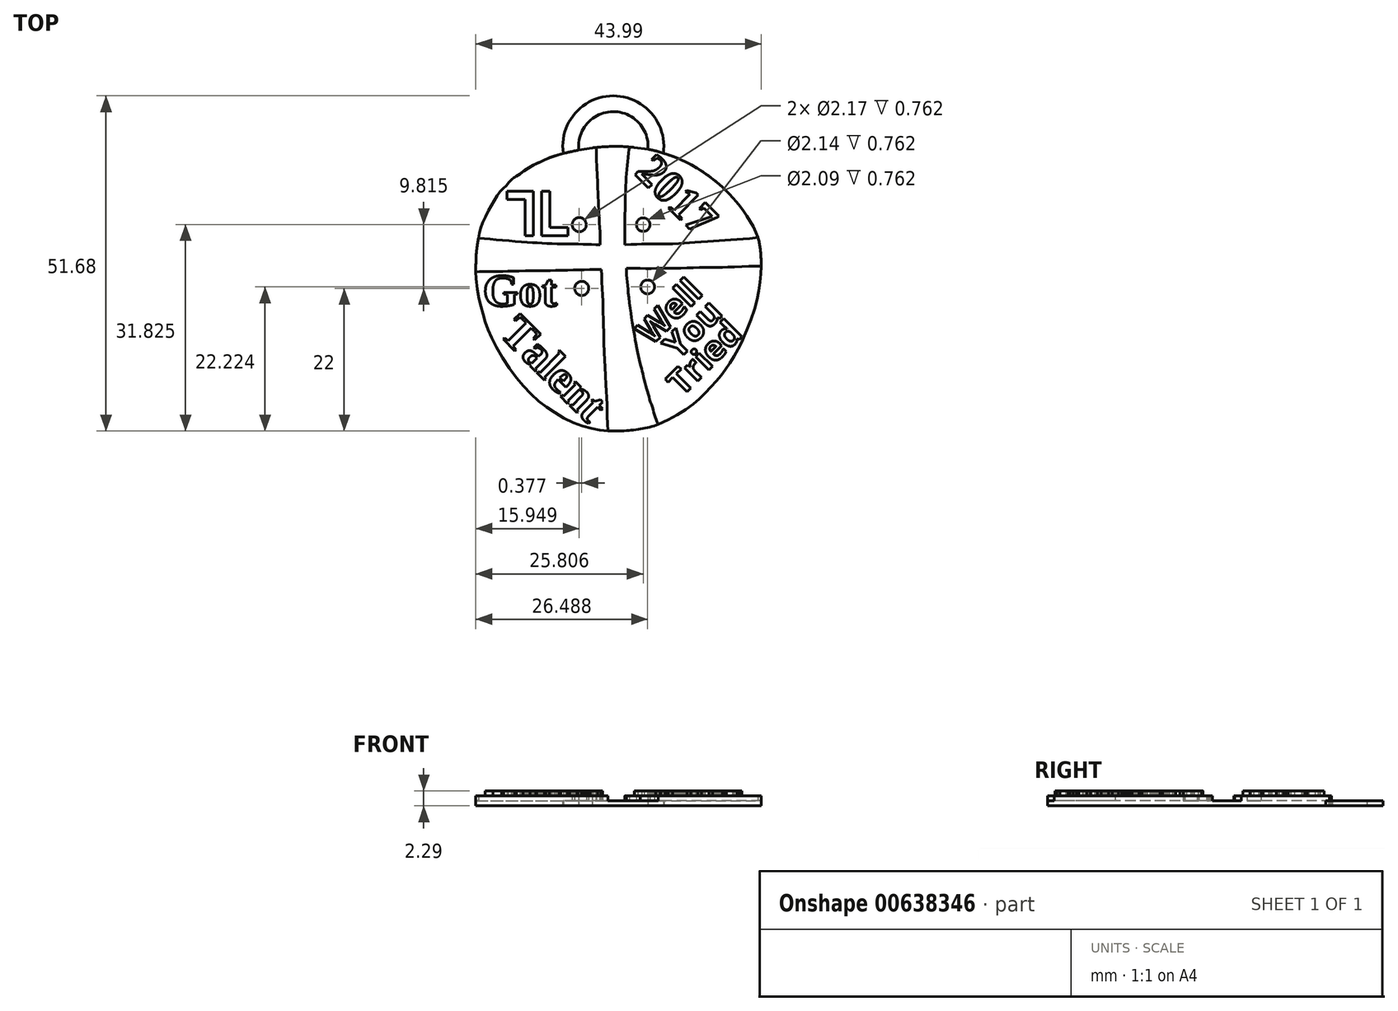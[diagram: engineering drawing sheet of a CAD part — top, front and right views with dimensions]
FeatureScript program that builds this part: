
annotation { "Feature Type Name" : "Feature", "Feature Type Description" : "" }
export const myFeature = defineFeature(function(context is Context, id is Id, definition is map)
    precondition{}
    {
        {
            var Q0;
            Q0=qCreatedBy(makeId("Top.planeOp"),FACE);
            var sketch = newSketch(context, id + "F0", { "sketchPlane" : qUnion([Q0])});
            skFitSpline(sketch, "E0", {"points": [v(-3.2, 18.94) * mm, v(-4.93, 18.73) * mm, v(-6.65, 18.38) * mm, v(-9.43, 17.71) * mm, v(-11.65, 16.8) * mm, v(-13.81, 15.7) * mm, v(-15.1, 14.79) * mm, v(-16.18, 14.06) * mm, v(-17.11, 13.04) * mm, v(-17.93, 12.28) * mm, v(-18.93, 10.84) * mm, v(-20, 8.91) * mm, v(-21.03, 6.49) * mm, v(-21.4, 4.95) * mm, v(-21.72, 2.6) * mm, v(-21.8, -0.22) * mm, v(-21.8, -0.23) * mm, v(-21.8, -0.23) * mm, v(-21.71, -1.8) * mm, v(-21.3, -4.51) * mm, v(-20.89, -6.04) * mm, v(-20.44, -7.64) * mm, v(-19.78, -9.41) * mm, v(-18.74, -11.67) * mm, v(-16.55, -15.21) * mm, v(-14.5, -17.79) * mm, v(-12.27, -20.05) * mm, v(-10.29, -21.5) * mm, v(-7.75, -23.03) * mm, v(-5.32, -24.04) * mm, v(-3.1, -24.6) * mm, v(-1.46, -24.77) * mm, v(2.16, -24.67) * mm, v(6.33, -23.76) * mm, v(9.35, -22.24) * mm, v(11.68, -20.7) * mm, v(13.1, -19.42) * mm, v(14.6, -17.86) * mm, v(15.74, -16.57) * mm, v(16.74, -15.22) * mm, v(17.75, -13.69) * mm, v(18.76, -11.92) * mm, v(19.49, -10.42) * mm, v(19.9, -9.38) * mm, v(21.17, -6.04) * mm, v(21.77, -3.53) * mm, v(22.08, -1.28) * mm, v(22.19, 0.62) * mm, v(22.1, 2.84) * mm, v(21.68, 5.05) * mm, v(20.34, 7.8) * mm, v(18.56, 10.32) * mm, v(16.99, 12.01) * mm, v(15.7, 13.25) * mm, v(13.81, 14.73) * mm, v(11.03, 16.46) * mm, v(8.11, 17.71) * mm, v(5.13, 18.58) * mm, v(1.93, 19) * mm, v(-0.6, 19.1) * mm, v(-3.2, 18.94) * mm]});
            skArc(sketch, "E1", {"start": v(4.73, 18.66) * mm, "mid": v(-0.67, 24.46) * mm, "end": v(-5.93, 18.54) * mm});
            skArc(sketch, "E2", {"start": v(7.1, 18.06) * mm, "mid": v(-0.63, 26.9) * mm, "end": v(-8.32, 18.01) * mm});
            skLineSegment(sketch, "E3", {"start": v(-5.93, 18.54) * mm, "end": v(-3.82, 18.88) * mm});
            skLineSegment(sketch, "E4", {"start": v(2.6, 18.94) * mm, "end": v(4.73, 18.66) * mm});
            skSolve(sketch);
        }
        {
            var Q0;
            Q0 = qSketchRegion(id + "F0", true);
            extrude(context, id + "F1", {"entities" : qUnion([Q0]), "depth" : 0.76 * mm, "offsetDistance" : 25.4 * mm});
        }
        {
            var Q0;
            Q0=makeQuery(id+"F1.opExtrude","CAP_FACE",FACE,{"disambiguationData":[OSD([sQuery(id+"F0.wireOp",EDGE,"E0")])],"isStart":false});
            var sketch = newSketch(context, id + "F2", { "sketchPlane" : qUnion([Q0])});
            skFitSpline(sketch, "E5", {"points": [v(-3.2, 18.94) * mm, v(-4.93, 18.73) * mm, v(-6.65, 18.38) * mm, v(-9.43, 17.71) * mm, v(-11.65, 16.8) * mm, v(-13.81, 15.7) * mm, v(-15.1, 14.79) * mm, v(-16.18, 14.06) * mm, v(-17.11, 13.04) * mm, v(-17.93, 12.28) * mm, v(-18.93, 10.84) * mm, v(-20, 8.91) * mm, v(-21.03, 6.49) * mm, v(-21.4, 4.95) * mm, v(-21.72, 2.6) * mm, v(-21.8, -0.22) * mm, v(-21.8, -0.23) * mm, v(-21.8, -0.23) * mm, v(-21.71, -1.8) * mm, v(-21.3, -4.51) * mm, v(-20.89, -6.04) * mm, v(-20.44, -7.64) * mm, v(-19.78, -9.41) * mm, v(-18.74, -11.67) * mm, v(-16.55, -15.21) * mm, v(-14.5, -17.79) * mm, v(-12.27, -20.05) * mm, v(-10.29, -21.5) * mm, v(-7.75, -23.03) * mm, v(-5.32, -24.04) * mm, v(-3.1, -24.6) * mm, v(-1.46, -24.77) * mm, v(2.16, -24.67) * mm, v(6.33, -23.76) * mm, v(9.35, -22.24) * mm, v(11.68, -20.7) * mm, v(13.1, -19.42) * mm, v(14.6, -17.86) * mm, v(15.74, -16.57) * mm, v(16.74, -15.22) * mm, v(17.75, -13.69) * mm, v(18.76, -11.92) * mm, v(19.49, -10.42) * mm, v(19.9, -9.38) * mm, v(21.17, -6.04) * mm, v(21.77, -3.53) * mm, v(22.08, -1.28) * mm, v(22.19, 0.62) * mm, v(22.1, 2.84) * mm, v(21.68, 5.05) * mm, v(20.34, 7.8) * mm, v(18.56, 10.32) * mm, v(16.99, 12.01) * mm, v(15.7, 13.25) * mm, v(13.81, 14.73) * mm, v(11.03, 16.46) * mm, v(8.11, 17.71) * mm, v(5.13, 18.58) * mm, v(1.93, 19) * mm, v(-0.6, 19.1) * mm, v(-3.2, 18.94) * mm]});
            skFitSpline(sketch, "E6", {"points": [v(-21.4, 4.95) * mm, v(-17.9, 4.65) * mm, v(-14.1, 4.33) * mm, v(-11.67, 4.19) * mm, v(-9.21, 4.07) * mm, v(-6.38, 4.04) * mm, v(-4.4, 3.98) * mm, v(-2.64, 3.92) * mm], "startDerivative": vector(20.38, -1.44) * mm, "endDerivative": vector(15, -0.48) * mm});
            skFitSpline(sketch, "E7", {"points": [v(-3.2, 18.94) * mm, v(-3.2, 16.96) * mm, v(-3.11, 15.45) * mm, v(-3.05, 14.12) * mm, v(-3, 12.68) * mm, v(-2.92, 11) * mm, v(-2.83, 9.25) * mm, v(-2.75, 7.56) * mm, v(-2.65, 5.66) * mm, v(-2.64, 3.92) * mm], "startDerivative": vector(-0.27, -16.84) * mm, "endDerivative": vector(-0.12, -15.04) * mm});
            skFitSpline(sketch, "E8", {"points": [v(1.93, 19) * mm, v(1.79, 18.41) * mm, v(1.61, 17.07) * mm, v(1.52, 15.95) * mm, v(1.4, 14.63) * mm, v(1.34, 13.3) * mm, v(1.25, 11.63) * mm, v(1.23, 9.85) * mm, v(1.17, 8.24) * mm, v(1.17, 6.74) * mm, v(1.17, 5.24) * mm, v(1.18, 3.92) * mm], "startDerivative": vector(-2.33, -8.47) * mm, "endDerivative": vector(0.1, -14.43) * mm});
            skFitSpline(sketch, "E9", {"points": [v(1.18, 3.92) * mm, v(2.92, 4) * mm, v(4.2, 4.03) * mm, v(5.44, 4.03) * mm, v(7.88, 4.06) * mm, v(9.82, 4.15) * mm, v(11.19, 4.25) * mm, v(12.96, 4.38) * mm, v(14.85, 4.5) * mm, v(16.43, 4.6) * mm, v(18.1, 4.74) * mm, v(20.21, 4.87) * mm, v(21.53, 5.02) * mm, v(21.68, 5.05) * mm], "startDerivative": vector(21.76, 1.06) * mm, "endDerivative": vector(6, 0.77) * mm});
            skFitSpline(sketch, "E10", {"points": [v(-21.8, -0.23) * mm, v(-20.73, -0.17) * mm, v(-19.36, -0.18) * mm, v(-17.32, -0.17) * mm, v(-15.12, -0.1) * mm, v(-11.79, -0.04) * mm, v(-9.68, -0.04) * mm, v(-7.15, 0.04) * mm, v(-4.95, 0.09) * mm, v(-2.43, 0.14) * mm], "startDerivative": vector(13.2, 1.01) * mm, "endDerivative": vector(20.6, 0.3) * mm});
            skFitSpline(sketch, "E11", {"points": [v(-2.43, 0.14) * mm, v(-2.36, -1.12) * mm, v(-2.35, -2.44) * mm, v(-2.28, -3.8) * mm, v(-2.22, -5.07) * mm, v(-2.23, -6.07) * mm, v(-2.18, -7.24) * mm, v(-2.13, -8.33) * mm, v(-2.04, -11.03) * mm, v(-1.94, -13.54) * mm, v(-1.87, -15.22) * mm, v(-1.74, -17.82) * mm, v(-1.65, -19.04) * mm, v(-1.6, -20.63) * mm, v(-1.57, -21.68) * mm, v(-1.5, -23.09) * mm, v(-1.46, -24.77) * mm], "startDerivative": vector(1.33, -22) * mm, "endDerivative": vector(0.62, -25.83) * mm});
            skFitSpline(sketch, "E12", {"points": [v(22.19, 0.62) * mm, v(20.29, 0.62) * mm, v(17.64, 0.5) * mm, v(15.92, 0.43) * mm, v(14.34, 0.42) * mm, v(12.48, 0.43) * mm, v(10.51, 0.34) * mm, v(8.76, 0.3) * mm, v(6.65, 0.3) * mm, v(5.13, 0.27) * mm, v(3.59, 0.28) * mm, v(2.45, 0.28) * mm, v(1.42, 0.28) * mm], "startDerivative": vector(-20.3, 0.28) * mm, "endDerivative": vector(-15.78, 0.1) * mm});
            skFitSpline(sketch, "E13", {"points": [v(1.42, 0.28) * mm, v(1.42, -0.35) * mm, v(1.5, -1.26) * mm, v(1.57, -2) * mm, v(1.65, -2.85) * mm, v(1.76, -4.02) * mm, v(2, -5.84) * mm, v(2.2, -7.42) * mm, v(2.47, -8.84) * mm, v(2.7, -10.17) * mm, v(2.86, -11.2) * mm, v(3.1, -12.38) * mm, v(3.31, -13.4) * mm, v(3.5, -14.38) * mm], "startDerivative": vector(-0.27, -10.35) * mm, "endDerivative": vector(4.5, -12.84) * mm});
            skFitSpline(sketch, "E14", {"points": [v(3.5, -14.38) * mm, v(3.8, -15.37) * mm, v(4.04, -16.41) * mm, v(4.42, -17.84) * mm, v(4.77, -18.95) * mm, v(5.03, -20.03) * mm, v(5.37, -21.02) * mm, v(5.67, -22.04) * mm, v(5.91, -22.82) * mm, v(6.33, -23.76) * mm], "startDerivative": vector(2.84, -9.2) * mm, "endDerivative": vector(4.17, -8.96) * mm});
            skCircle(sketch, "E15", {"center": v(-5.85, 7.03) * mm, "radius": 1.09 * mm});
            skCircle(sketch, "E16", {"center": v(4, 7.04) * mm, "radius": 1.05 * mm});
            skCircle(sketch, "E17", {"center": v(4.69, -2.57) * mm, "radius": 1.07 * mm});
            skCircle(sketch, "E18", {"center": v(-5.47, -2.79) * mm, "radius": 1.08 * mm});
            skSolve(sketch);
        }
        {
            var Q0;
            {var subQ0=sQuery(id+"F2.wireOp",EDGE,"E6");Q0=makeQuery(id+"F2.imprint","IMPRINT",FACE,{"disambiguationData":[TD([[makeQuery(id+"F2.imprint","IMPRINT",EDGE,{"derivedFrom":subQ0}),1.0]])]});}
            var Q1;
            {var subQ0=sQuery(id+"F2.wireOp",EDGE,"E8");Q1=makeQuery(id+"F2.imprint","IMPRINT",FACE,{"disambiguationData":[TD([[makeQuery(id+"F2.imprint","IMPRINT",EDGE,{"derivedFrom":subQ0}),1.0]])]});}
            var Q2;
            {var subQ1=sQuery(id+"F2.wireOp",EDGE,"E12");Q2=makeQuery(id+"F2.imprint","IMPRINT",FACE,{"disambiguationData":[TD([[makeQuery(id+"F2.imprint","IMPRINT",EDGE,{"derivedFrom":subQ1}),1.0]])]});}
            var Q3;
            {var subQ0=sQuery(id+"F2.wireOp",EDGE,"E10");Q3=makeQuery(id+"F2.imprint","IMPRINT",FACE,{"disambiguationData":[TD([[makeQuery(id+"F2.imprint","IMPRINT",EDGE,{"derivedFrom":subQ0}),-1.0]])]});}
            extrude(context, id + "F3", {"entities" : qUnion([Q0, Q1, Q2, Q3]), "operationType" : NewBodyOperationType.ADD, "depth" : 0.76 * mm, "offsetDistance" : 25.4 * mm});
        }
        {
            var Q0;
            Q0=makeQuery(id+"F3.opExtrude","CAP_FACE",FACE,{"disambiguationData":[OSD([sQuery(id+"F2.wireOp",EDGE,"E5"),sQuery(id+"F2.wireOp",EDGE,"E8"),sQuery(id+"F2.wireOp",EDGE,"E9"),sQuery(id+"F2.wireOp",EDGE,"E16")])],"isStart":false});
            var sketch = newSketch(context, id + "F4", { "sketchPlane" : qUnion([Q0])});
            skText(sketch, "E19", { "text": "2017", "fontName": "Tinos-Bold.ttf"});
            const initialGuessF4  = {"E19": [0.00254, 0.01496, 0.7071, -0.7071, 0.00508]};
            skSetInitialGuess(sketch, initialGuessF4);
            skSolve(sketch);
        }
        {
            var Q0;
            Q0=makeQuery(id+"F3.opExtrude","CAP_FACE",FACE,{"disambiguationData":[OSD([sQuery(id+"F2.wireOp",EDGE,"E5"),sQuery(id+"F2.wireOp",EDGE,"E10"),sQuery(id+"F2.wireOp",EDGE,"E11"),sQuery(id+"F2.wireOp",EDGE,"E18")])],"isStart":false});
            var sketch = newSketch(context, id + "F5", { "sketchPlane" : qUnion([Q0])});
            skText(sketch, "E20", { "text": "Got", "fontName": "Tinos-Bold.ttf"});
            skText(sketch, "E21", { "text": "Talent", "fontName": "Tinos-Bold.ttf"});
            const initialGuessF5  = {"E20": [-0.02067, -0.0055, 1, 0, 0.00508], "E21": [-0.01832, -0.00986, 0.7071, -0.7071, 0.00508]};
            skSetInitialGuess(sketch, initialGuessF5);
            skSolve(sketch);
        }
        {
            var Q0;
            Q0=makeQuery(id+"F3.opExtrude","CAP_FACE",FACE,{"disambiguationData":[OSD([sQuery(id+"F2.wireOp",EDGE,"E5"),sQuery(id+"F2.wireOp",EDGE,"E12"),sQuery(id+"F2.wireOp",EDGE,"E13"),sQuery(id+"F2.wireOp",EDGE,"E14"),sQuery(id+"F2.wireOp",EDGE,"E17")])],"isStart":false});
            var sketch = newSketch(context, id + "F6", { "sketchPlane" : qUnion([Q0])});
            skText(sketch, "E22", { "text": "Well", "fontName": "OpenSans-Bold.ttf"});
            skText(sketch, "E23", { "text": "You", "fontName": "OpenSans-Bold.ttf"});
            skText(sketch, "E24", { "text": "Tried", "fontName": "OpenSans-Bold.ttf"});
            const initialGuessF6  = {"E22": [0.00528, -0.01169, 0.7071, 0.7071, 0.00381], "E23": [0.00936, -0.01388, 0.7071, 0.7071, 0.0038], "E24": [0.00996, -0.01953, 0.7071, 0.7071, 0.0038]};
            skSetInitialGuess(sketch, initialGuessF6);
            skSolve(sketch);
        }
        {
            var Q0;
            Q0=makeQuery(id+"F3.opExtrude","CAP_FACE",FACE,{"disambiguationData":[OSD([sQuery(id+"F2.wireOp",EDGE,"E5"),sQuery(id+"F2.wireOp",EDGE,"E6"),sQuery(id+"F2.wireOp",EDGE,"E7"),sQuery(id+"F2.wireOp",EDGE,"E15")])],"isStart":false});
            var sketch = newSketch(context, id + "F7", { "sketchPlane" : qUnion([Q0])});
            skLineSegment(sketch, "E25", {"start": v(-11.68, 12.2) * mm, "end": v(-11.68, 5.33) * mm});
            skLineSegment(sketch, "E26", {"start": v(-11.68, 5.33) * mm, "end": v(-7.62, 5.33) * mm});
            skLineSegment(sketch, "E27", {"start": v(-7.62, 5.33) * mm, "end": v(-7.62, 6.6) * mm});
            skLineSegment(sketch, "E28", {"start": v(-7.62, 6.6) * mm, "end": v(-10.41, 6.6) * mm});
            skLineSegment(sketch, "E29", {"start": v(-10.41, 6.6) * mm, "end": v(-10.41, 12.2) * mm});
            skLineSegment(sketch, "E30", {"start": v(-10.41, 12.2) * mm, "end": v(-11.68, 12.2) * mm});
            skLineSegment(sketch, "E31", {"start": v(-12.95, 12.2) * mm, "end": v(-12.95, 5.33) * mm});
            skLineSegment(sketch, "E32", {"start": v(-12.95, 5.33) * mm, "end": v(-14.22, 5.33) * mm});
            skLineSegment(sketch, "E33", {"start": v(-14.22, 5.33) * mm, "end": v(-14.22, 10.92) * mm});
            skLineSegment(sketch, "E34", {"start": v(-14.22, 10.92) * mm, "end": v(-17.02, 10.92) * mm});
            skLineSegment(sketch, "E35", {"start": v(-17.02, 10.92) * mm, "end": v(-17.02, 12.2) * mm});
            skLineSegment(sketch, "E36", {"start": v(-17.02, 12.2) * mm, "end": v(-12.95, 12.2) * mm});
            skSolve(sketch);
        }
        {
            var Q0;
            Q0 = qSketchRegion(id + "F4", true);
            var Q1;
            Q1 = qSketchRegion(id + "F5", true);
            var Q2;
            Q2 = qSketchRegion(id + "F6", true);
            var Q3;
            Q3 = qSketchRegion(id + "F7", true);
            extrude(context, id + "F8", {"entities" : qUnion([Q0, Q1, Q2, Q3]), "operationType" : NewBodyOperationType.ADD, "depth" : 0.76 * mm, "offsetDistance" : 25.4 * mm});
        }
    });
